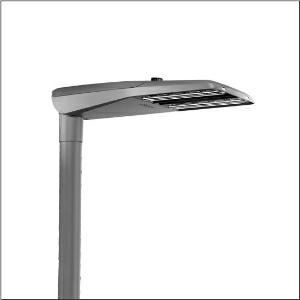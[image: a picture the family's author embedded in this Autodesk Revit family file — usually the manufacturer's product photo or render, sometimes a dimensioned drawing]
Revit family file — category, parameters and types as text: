
# Revit family: streetlight_sl_11_iq_midi___st1_2a_5xc3a41u08me_4bff
name_source: partatom
category: Lighting Fixtures
units: mm (PartAtom-declared; Revit-internal decimal feet)

## family parameters
Cut with Voids When Loaded = No
Host = Face
Light Source = No
Part Type = Normal
Room Calculation Point = No
Round Connector Dimension = Use Diameter
Shared = No

## types (1)
- --- (1 x LED, 18900 lm, 122.6 W, 4000K)
    Apparent Load = 123 VA
    CIE Flux Codes = 32 70 96 100 100
    Color Rendering = 70
    Color Temperature = 4000K
    Default Elevation = 1800 mm
    Description = Streetlight SL 11 iQ midi, mast luminaire, primary light control with 3 zone facetted reflector, of plastic, silver coated, highly specular, primary optical cover: cover, of PMMA, transparent, light distribution: ST1.2a, light emission: direct distribution, primary light characteristic: asymmetric, installation type: post-top, side-entry, LED, High Power LED, rated luminous flux: 18.900lm, luminous efficacy: 154lm/W, light colour: 740, colour temperature: 4000K, control: presetting dimming logarithmic, Street-Remote, Auto-Match, Temp-Guard, Lumen-Switch, Night-Set, Smart-Wire, Light-Fading, Desk-Remote (wireless, voltage-free reading and setting of iQ features in the workshop via application-optimized NFC function/RFID function), optimised constant luminous flux control (CLO 2.0), with cable H07RN-F 5x 1.5mm², mains connection: 230..240V, AC, 50/60Hz, connection cable pre-assembled, cable length: 12,5m, start of lifetime: 123W, end of service life: 130W, reduction: 56W, luminaire housing, of diecast aluminium, powder-coated, Siteco® metallic grey (DB 702S), please order mast flange separately, inclination adjustable without tools: 0°, 5°, 10°, 15° (post-top) | 0°, -5°, -10°, -15° (side-entry), sealing non-destructively replaceable, multi-level sealing system, length: 780mm, width: 376mm, height: 118mm, mast flange for spigot size: 42mm (side-entry): 5XC10008XM4, 60/48mm (side-entry/post-top): 5XC10108XM2, 76/60mm (side-entry/post-top): 5XC10108XM1, equipment: Power, Smart Interface below, protection rating (complete): IP66, insulation class (complete): insulation class II (safety insulation), certification: CE, ENEC, VDE, UKCA, impact resistance: IK09, permissible operating ambient temperature for outdoor applications: -25..+50°C, standard-compliant lighting for roads and squares, Environmental Product Declaration (EPD) tested and certified by an independent institute, packaging unit: 1 piece

Light Distribution: ST1.2a
    Height = 118 mm
    Lamp = 1 x LED
    Lamp Light Flux = 18900 lm
    Lamp Power = 122.6 W
    Lamp count = 1
    Length = 780 mm
    Luminous efficacy = 154 lm/W
    Manufacturer = Siteco
    ModVariant = No
    Model = 5XC3A41U08ME
    Number of Poles = 1
    OnlyDefault = Yes
    Power Factor = 1
    Product Name = Streetlight SL 11 iQ midi | ST1.2a
    Product group = mast luminaire | pylon top
    ProductGroupID = 6100
    Protection Class = Protection class II
    Protection Degree = IP 66
    RLX_Detail_Level = 1
    RLX_Emergency_Light_Flux = 0 lm
    RLX_Emergency_Type = 0
    RLX_Emergency_Type_DB = No
    RlxData = <blob elided: 69685 chars, md5=acb25591>
    Socket = socket
    Standby Power = 0 W
    System Light Flux = 18900 lm
    System Power = 123 W
    Type Comments = factory setting: luminous flux: 100 % | dim-lin: 254 | 552 mA
    Type Image = l_1005968.jpg
    URL = http://relux.com
    VarID = @adj_082453
    Voltage = 0 V
    Weight = 0.00 kg
    Width = 376 mm

## geometry (parser evidence)
native form markers: Blend x4, Sweep x9
no freeform markers — native parametric forms only
